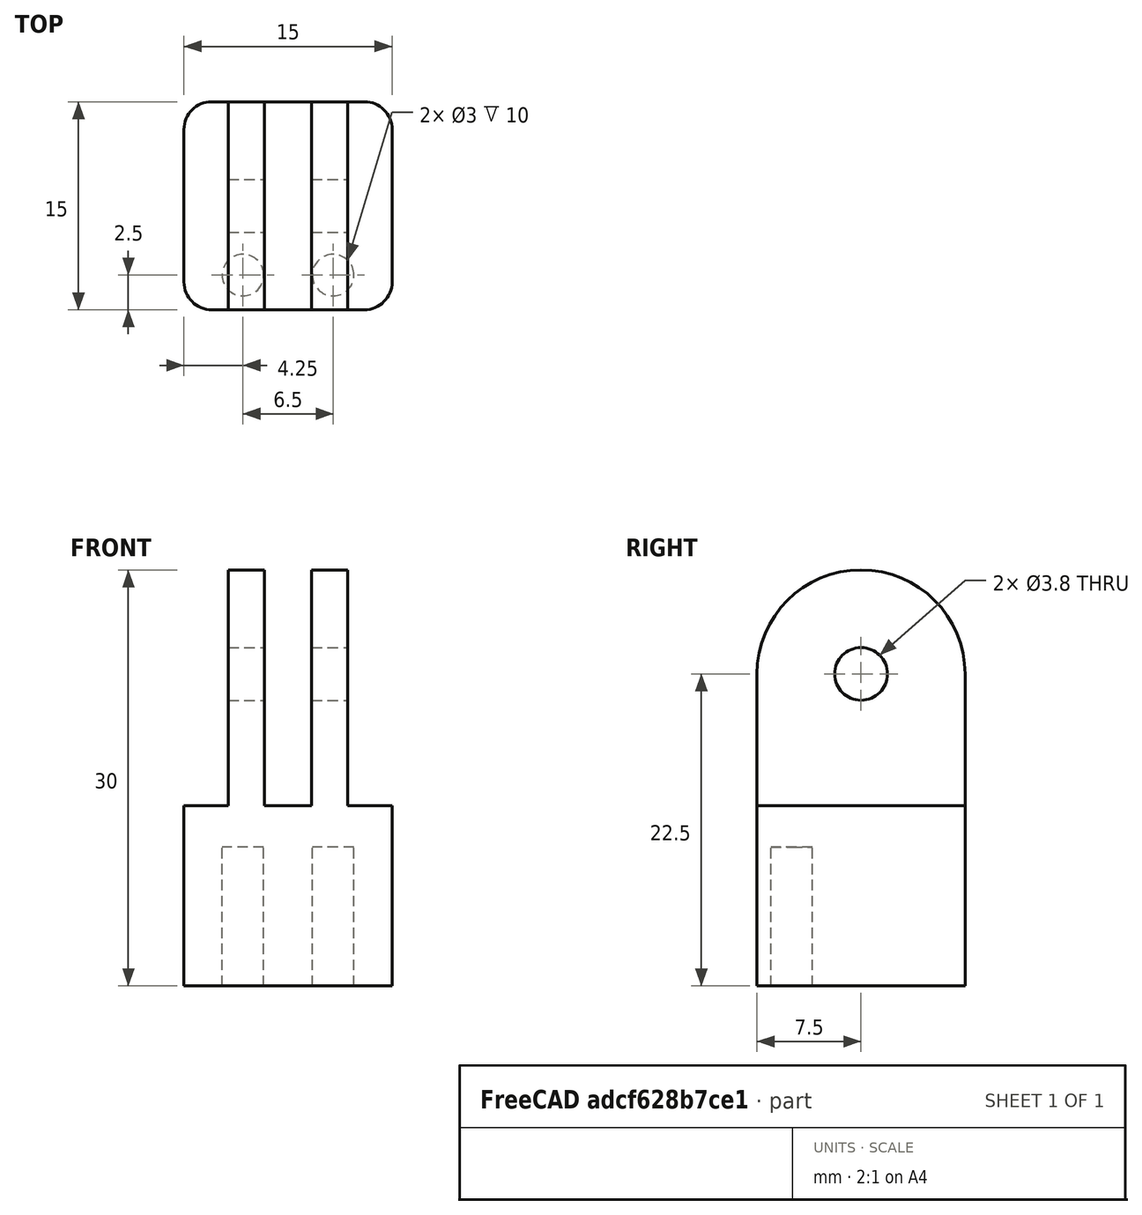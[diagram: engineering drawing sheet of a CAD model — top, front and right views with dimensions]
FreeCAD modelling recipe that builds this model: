
FCSTD DOCUMENT  (FreeCAD 0.19R23578 (Git))
Label: UV_CJMCU_sensor
License: FreeArt
LicenseURL: http://artlibre.org/licence/lal
objects: Spreadsheet::Sheet×1, Part::Cylinder×1, Part::FeaturePython×1, Part::Box×1, Part::Feature×1, Part::MultiFuse×1, Part::Cut×1, Part::Fillet×1, App::Part×1
note: 7 computed .brp shape members not serialized (recipe doc carries the construction recipe); baked Part::Feature solids carry a one-line shape summary decoded from their .brp

FEATURE [Spreadsheet::Sheet] Spreadsheet  label="p"
  cells = A1=pcb_x; B1(pcb_x)=11.2; A2=pcb_y; B2(pcb_y)=28; A3=pcb_z; B3(pcb_z)=1.7; A4=hole_dist_x; B4(hole_dist_x)=6.5; A5=hole_off_y; B5(hole_off_y)=2.5; A6=hole_r; B6(hole_r)=1.5; A7=wall; B7(wall)=3; A8=stick_x; B8(stick_x)=15; A9=stick_y; B9(stick_y)=15; A10=stick_length; B10(stick_length)=10
FEATURE [Part::Cylinder] Cylinder  label="bolt hole"
  Angle = 360
  AttacherType = Attacher::AttachEngine3D
  Height = 10
  Radius = 1.5
  expr: Radius = <<p>>.hole_r
FEATURE [Part::FeaturePython] Array  label="bolt hole array"  # Draft array (typed FeaturePython)
  Angle = 360
  ArrayType = 0
  Axis = (0,0,1)
  Base = -> Cylinder
  Center = (0,0,0)
  Fuse = false
  IntervalAxis = (0,0,0)
  IntervalX = (6.5,0,0)
  IntervalY = (0,1,0)
  IntervalZ = (0,0,1)
  NumberPolar = 1
  NumberX = 2
  NumberY = 1
  NumberZ = 1
  Placement = pos=(4.25,2.5,0) rot=(0,0,1;0rad)
  expr: .Placement.Base.x = (max(<<p>>.pcb_x; <<p>>.stick_x) - <<p>>.hole_dist_x) / 2
  expr: .IntervalX.x = <<p>>.hole_dist_x
  expr: .Placement.Base.y = <<p>>.hole_off_y
FEATURE [Part::Box] Box002  label="stick cube"
  AttacherType = Attacher::AttachEngine3D
  Height = 10
  Length = 15
  Width = 15
  expr: Length = <<p>>.stick_x
  expr: Width = <<p>>.stick_y
  expr: Height = <<p>>.stick_length
FEATURE [Part::Feature] Cut001001  label="side 2 cut001"
  Placement = pos=(7.5,7.5,10) rot=(0,0,1;1.5708rad)
  shape: bbox 15 x 15 x 20 mm, 16 faces (baked)
  expr: .Placement.Base.y = <<p>>.stick_y / 2
  expr: .Placement.Base.x = Spreadsheet.stick_x / 2
  expr: .Placement.Base.z = <<p>>.stick_length
FEATURE [Part::MultiFuse] Fusion  label="holder fusion"
  Shapes = -> [Cut001001,Box002]
FEATURE [Part::Cut] Cut  label="sensor cut"
  Base = -> Fusion
  Tool = -> Array
FEATURE [Part::Fillet] Fillet  label="sensor fillet"
  Base = -> Cut
  Edges = 8 edges r=2: [Edge1,Edge3,Edge6,Edge8,Edge10,Edge12,Edge18,Edge28]
FEATURE [App::Part] Part  label="TCS3472 sensor part"
  Group = -> [Cut,Cut001001,Fusion,Array,Cylinder,Box002,Fillet]
  Origin = -> Origin
